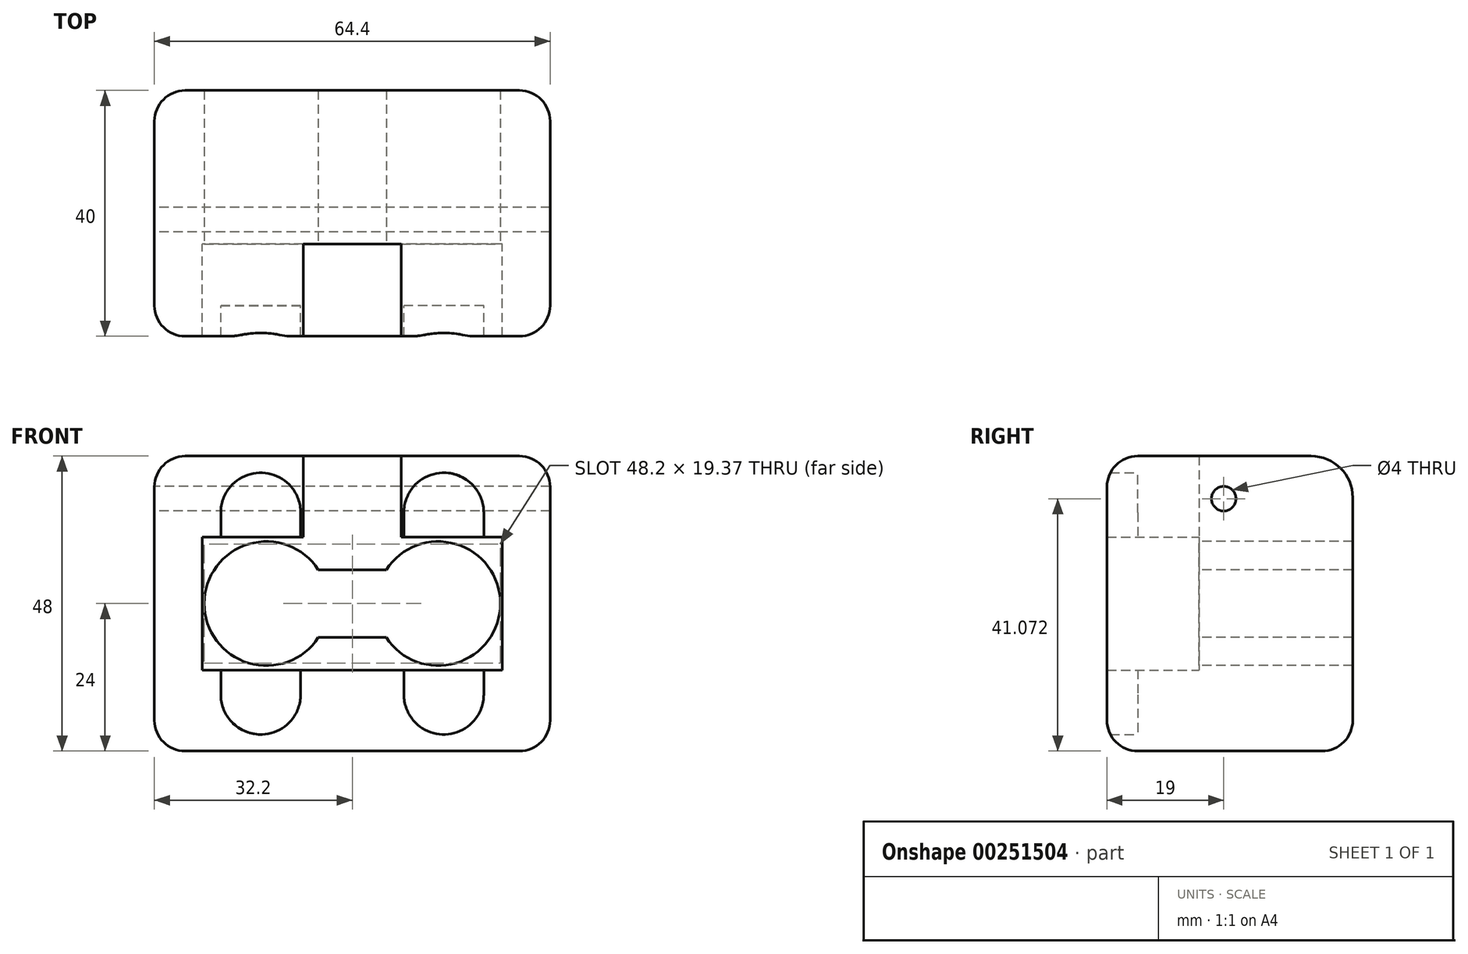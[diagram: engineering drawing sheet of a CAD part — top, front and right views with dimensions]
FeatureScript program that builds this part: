
annotation { "Feature Type Name" : "Feature", "Feature Type Description" : "" }
export const myFeature = defineFeature(function(context is Context, id is Id, definition is map)
    precondition{}
    {
        {
            var Q0;
            Q0=qCreatedBy(makeId("Front.planeOp"),FACE);
            var sketch = newSketch(context, id + "F0", { "sketchPlane" : qUnion([Q0])});
            skLineSegment(sketch, "E0.bottom", {"start": v(32.2, 24) * mm, "end": v(-32.2, 24) * mm});
            skLineSegment(sketch, "E0.top", {"start": v(32.2, -24) * mm, "end": v(-32.2, -24) * mm});
            skLineSegment(sketch, "E0.left", {"start": v(32.2, 24) * mm, "end": v(32.2, -24) * mm});
            skLineSegment(sketch, "E0.right", {"start": v(-32.2, 24) * mm, "end": v(-32.2, -24) * mm});
            skPoint(sketch, "E0.middle", {"position": v(0, 0) * mm});
            skLineSegment(sketch, "E1.bottom", {"start": v(24.4, 10.8) * mm, "end": v(21.4, 10.8) * mm});
            skLineSegment(sketch, "E1.top", {"start": v(24.4, -10.8) * mm, "end": v(21.4, -10.8) * mm});
            skLineSegment(sketch, "E1.left", {"start": v(24.4, 10.8) * mm, "end": v(24.4, -10.8) * mm});
            skLineSegment(sketch, "E1.right", {"start": v(-24.4, 10.8) * mm, "end": v(-24.4, -10.8) * mm});
            skLineSegment(sketch, "E2", {"start": v(-8, 24) * mm, "end": v(-8, 10.8) * mm});
            skPoint(sketch, "E3", {"position": v(0, 24) * mm});
            skLineSegment(sketch, "E4.MirrorCS", {"start": v(8, 24) * mm, "end": v(8, 10.8) * mm});
            skLineSegment(sketch, "E5", {"start": v(-21.4, 10.8) * mm, "end": v(-21.4, 14.8) * mm});
            skLineSegment(sketch, "E6", {"start": v(-8.4, 14.8) * mm, "end": v(-8.4, 10.8) * mm});
            skArc(sketch, "E7", {"start": v(-8.4, 14.8) * mm, "mid": v(-14.9, 21.3) * mm, "end": v(-21.4, 14.8) * mm});
            skLineSegment(sketch, "E8.trimOffspring", {"start": v(-21.4, 10.8) * mm, "end": v(-24.4, 10.8) * mm});
            skLineSegment(sketch, "E9.MirrorCS", {"start": v(21.4, 10.8) * mm, "end": v(21.4, 14.8) * mm});
            skArc(sketch, "E10.MirrorCS", {"start": v(8.4, 14.8) * mm, "mid": v(14.9, 21.3) * mm, "end": v(21.4, 14.8) * mm});
            skLineSegment(sketch, "E11.MirrorCS", {"start": v(8.4, 14.8) * mm, "end": v(8.4, 10.8) * mm});
            skLineSegment(sketch, "E12.MirrorCS", {"start": v(-21.4, -10.8) * mm, "end": v(-21.4, -14.8) * mm});
            skArc(sketch, "E13.MirrorCS", {"start": v(-8.4, -14.8) * mm, "mid": v(-14.9, -21.3) * mm, "end": v(-21.4, -14.8) * mm});
            skLineSegment(sketch, "E14.MirrorCS", {"start": v(-8.4, -14.8) * mm, "end": v(-8.4, -10.8) * mm});
            skLineSegment(sketch, "E15.MirrorCS", {"start": v(8.4, -14.8) * mm, "end": v(8.4, -10.8) * mm});
            skArc(sketch, "E16.MirrorCS", {"start": v(8.4, -14.8) * mm, "mid": v(14.9, -21.3) * mm, "end": v(21.4, -14.8) * mm});
            skLineSegment(sketch, "E17.MirrorCS", {"start": v(21.4, -10.8) * mm, "end": v(21.4, -14.8) * mm});
            skLineSegment(sketch, "E18.trimOffspring", {"start": v(8.4, 10.8) * mm, "end": v(8, 10.8) * mm});
            skLineSegment(sketch, "E19.trimOffspring", {"start": v(8.4, -10.8) * mm, "end": v(-8.4, -10.8) * mm});
            skLineSegment(sketch, "E20.trimOffspring", {"start": v(-21.4, -10.8) * mm, "end": v(-24.4, -10.8) * mm});
            skLineSegment(sketch, "E21.trimOffspring", {"start": v(-8, 10.8) * mm, "end": v(-8.4, 10.8) * mm});
            skSolve(sketch);
        }
        {
            var Q0;
            Q0=makeQuery(id+"F0.imprint","IMPRINT",FACE,{"disambiguationData":[TD([[makeQuery(id+"F0.imprint","IMPRINT",EDGE,{"derivedFrom":sQuery(id+"F0.wireOp",EDGE,"E0.top")}),-1.0]])]});
            extrude(context, id + "F1", {"entities" : qUnion([Q0]), "flatOperationType" : FlatOperationType.REMOVE, "offsetDistance" : 25 * mm, "depth" : 5 * mm, "domain" : OperationDomain.MODEL});
        }
        {
            var Q0;
            Q0=makeQuery(id+"F1.opExtrude","CAP_FACE",FACE,{"disambiguationData":[OSD([sQuery(id+"F0.wireOp",EDGE,"E0.bottom"),sQuery(id+"F0.wireOp",EDGE,"E0.top"),sQuery(id+"F0.wireOp",EDGE,"E0.left"),sQuery(id+"F0.wireOp",EDGE,"E0.right"),sQuery(id+"F0.wireOp",EDGE,"E1.bottom"),sQuery(id+"F0.wireOp",EDGE,"E1.top"),sQuery(id+"F0.wireOp",EDGE,"E1.left"),sQuery(id+"F0.wireOp",EDGE,"E1.right"),sQuery(id+"F0.wireOp",EDGE,"E2"),sQuery(id+"F0.wireOp",EDGE,"E4.MirrorCS"),sQuery(id+"F0.wireOp",EDGE,"E5"),sQuery(id+"F0.wireOp",EDGE,"E6"),sQuery(id+"F0.wireOp",EDGE,"E7"),sQuery(id+"F0.wireOp",EDGE,"E8.trimOffspring"),sQuery(id+"F0.wireOp",EDGE,"E9.MirrorCS"),sQuery(id+"F0.wireOp",EDGE,"E10.MirrorCS"),sQuery(id+"F0.wireOp",EDGE,"E11.MirrorCS"),sQuery(id+"F0.wireOp",EDGE,"E12.MirrorCS"),sQuery(id+"F0.wireOp",EDGE,"E13.MirrorCS"),sQuery(id+"F0.wireOp",EDGE,"E14.MirrorCS"),sQuery(id+"F0.wireOp",EDGE,"E15.MirrorCS"),sQuery(id+"F0.wireOp",EDGE,"E16.MirrorCS"),sQuery(id+"F0.wireOp",EDGE,"E17.MirrorCS"),sQuery(id+"F0.wireOp",EDGE,"E18.trimOffspring"),sQuery(id+"F0.wireOp",EDGE,"E19.trimOffspring"),sQuery(id+"F0.wireOp",EDGE,"E20.trimOffspring"),sQuery(id+"F0.wireOp",EDGE,"E21.trimOffspring")])],"isStart":true});
            var sketch = newSketch(context, id + "F2", { "sketchPlane" : qUnion([Q0])});
            skLineSegment(sketch, "E22.bottom", {"start": v(24.4, -10.8) * mm, "end": v(-24.4, -10.8) * mm});
            skLineSegment(sketch, "E22.top", {"start": v(24.4, 10.8) * mm, "end": v(-24.4, 10.8) * mm});
            skLineSegment(sketch, "E22.left", {"start": v(24.4, -10.8) * mm, "end": v(24.4, 10.8) * mm});
            skLineSegment(sketch, "E22.right", {"start": v(-24.4, -10.8) * mm, "end": v(-24.4, 10.8) * mm});
            skPoint(sketch, "E22.middle", {"position": v(0, 0) * mm});
            skLineSegment(sketch, "E23.bottom", {"start": v(-32.2, 24) * mm, "end": v(32.2, 24) * mm});
            skLineSegment(sketch, "E23.top", {"start": v(-32.2, -24) * mm, "end": v(32.2, -24) * mm});
            skLineSegment(sketch, "E23.left", {"start": v(-32.2, 24) * mm, "end": v(-32.2, -24) * mm});
            skLineSegment(sketch, "E23.right", {"start": v(32.2, 24) * mm, "end": v(32.2, -24) * mm});
            skLineSegment(sketch, "E24", {"start": v(8, 10.8) * mm, "end": v(8, 24) * mm});
            skLineSegment(sketch, "E25", {"start": v(-8, 10.8) * mm, "end": v(-8, 24) * mm});
            skSolve(sketch);
        }
        {
            var Q0;
            {var subQ12=sQuery(id+"F2.wireOp",EDGE,"E22.left");Q0=makeQuery(id+"F2.imprint","IMPRINT",FACE,{"disambiguationData":[TD([[makeQuery(id+"F2.imprint","IMPRINT",EDGE,{"derivedFrom":subQ12}),1.0]])]});}
            var Q1;
            {var subQ1=makeQuery(id+"F1.opExtrude","CAP_EDGE",EDGE,{"disambiguationData":[OSD([sQuery(id+"F0.wireOp",EDGE,"E12.MirrorCS")])],"isStart":true});Q1=makeQuery(id+"F2.imprint","IMPRINT",FACE,{"disambiguationData":[TD([[makeQuery(id+"F2.imprint","IMPRINT",EDGE,{"derivedFrom":subQ1}),-1.0]])]});}
            var Q2;
            {var subQ2=makeQuery(id+"F1.opExtrude","CAP_EDGE",EDGE,{"disambiguationData":[OSD([sQuery(id+"F0.wireOp",EDGE,"E15.MirrorCS")])],"isStart":true});Q2=makeQuery(id+"F2.imprint","IMPRINT",FACE,{"disambiguationData":[TD([[makeQuery(id+"F2.imprint","IMPRINT",EDGE,{"derivedFrom":subQ2}),1.0]])]});}
            var Q3;
            {var subQ1=makeQuery(id+"F1.opExtrude","CAP_EDGE",EDGE,{"disambiguationData":[OSD([sQuery(id+"F0.wireOp",EDGE,"E5")])],"isStart":true});Q3=makeQuery(id+"F2.imprint","IMPRINT",FACE,{"disambiguationData":[TD([[makeQuery(id+"F2.imprint","IMPRINT",EDGE,{"derivedFrom":subQ1}),1.0]])]});}
            var Q4;
            {var subQ1=makeQuery(id+"F1.opExtrude","CAP_EDGE",EDGE,{"disambiguationData":[OSD([sQuery(id+"F0.wireOp",EDGE,"E9.MirrorCS")])],"isStart":true});Q4=makeQuery(id+"F2.imprint","IMPRINT",FACE,{"disambiguationData":[TD([[makeQuery(id+"F2.imprint","IMPRINT",EDGE,{"derivedFrom":subQ1}),-1.0]])]});}
            extrude(context, id + "F3", {"entities" : qUnion([Q0, Q1, Q2, Q3, Q4]), "operationType" : NewBodyOperationType.ADD, "depth" : 10 * mm});
        }
        {
            var Q0;
            Q0=makeQuery(id+"F3.opExtrude","CAP_FACE",FACE,{"disambiguationData":[OSD([sQuery(id+"F2.wireOp",EDGE,"E22.bottom"),sQuery(id+"F2.wireOp",EDGE,"E22.top"),sQuery(id+"F2.wireOp",EDGE,"E22.left"),sQuery(id+"F2.wireOp",EDGE,"E22.right"),sQuery(id+"F2.wireOp",EDGE,"E23.bottom"),sQuery(id+"F2.wireOp",EDGE,"E23.top"),sQuery(id+"F2.wireOp",EDGE,"E23.left"),sQuery(id+"F2.wireOp",EDGE,"E23.right"),sQuery(id+"F2.wireOp",EDGE,"E24"),sQuery(id+"F2.wireOp",EDGE,"E25")])],"isStart":false});
            var sketch = newSketch(context, id + "F4", { "sketchPlane" : qUnion([Q0])});
            skCircle(sketch, "E26", {"center": v(14, 0) * mm, "radius": 10.1 * mm});
            skLineSegment(sketch, "E27", {"start": v(5.53, -5.5) * mm, "end": v(0, -5.5) * mm});
            skLineSegment(sketch, "E28.MirrorCS", {"start": v(5.53, 5.5) * mm, "end": v(0, 5.5) * mm});
            skCircle(sketch, "E29.MirrorC", {"center": v(-14, 0) * mm, "radius": 10.1 * mm});
            skLineSegment(sketch, "E30.MirrorCS", {"start": v(-5.53, -5.5) * mm, "end": v(0, -5.5) * mm});
            skLineSegment(sketch, "E31.MirrorCS", {"start": v(-5.53, 5.5) * mm, "end": v(0, 5.5) * mm});
            skLineSegment(sketch, "E32.bottom", {"start": v(32.2, 24) * mm, "end": v(-32.2, 24) * mm});
            skLineSegment(sketch, "E32.top", {"start": v(32.2, -24) * mm, "end": v(-32.2, -24) * mm});
            skLineSegment(sketch, "E32.left", {"start": v(32.2, 24) * mm, "end": v(32.2, -24) * mm});
            skLineSegment(sketch, "E32.right", {"start": v(-32.2, 24) * mm, "end": v(-32.2, -24) * mm});
            skPoint(sketch, "E32.middle", {"position": v(0, 0) * mm});
            skSolve(sketch);
        }
        {
            var Q0;
            Q0=makeQuery(id+"F4.imprint","IMPRINT",FACE,{"disambiguationData":[TD([[makeQuery(id+"F4.imprint","IMPRINT",EDGE,{"derivedFrom":sQuery(id+"F4.wireOp",EDGE,"E32.top")}),1.0]])]});
            var Q1;
            {var subQ10=sQuery(id+"F4.wireOp",EDGE,"E27");Q1=makeQuery(id+"F4.imprint","IMPRINT",FACE,{"disambiguationData":[TD([[makeQuery(id+"F4.imprint","IMPRINT",EDGE,{"derivedFrom":subQ10}),1.0]])]});}
            extrude(context, id + "F5", {"entities" : qUnion([Q0, Q1]), "operationType" : NewBodyOperationType.ADD, "depth" : 25 * mm});
        }
        {
            var Q0;
            Q0=makeQuery(id+"F5.boolean.opBoolean","MERGE",FACE,{"derivedFrom":[makeQuery(id+"F3.boolean.opBoolean","MERGE",FACE,{"derivedFrom":[makeQuery(id+"F1.opExtrude","SWEPT_FACE",FACE,{"disambiguationData":[OSD([sQuery(id+"F0.wireOp",EDGE,"E0.right")])]}),makeQuery(id+"F3.opExtrude","SWEPT_FACE",FACE,{"disambiguationData":[OSD([sQuery(id+"F2.wireOp",EDGE,"E23.right")])]})]}),makeQuery(id+"F5.opExtrude","SWEPT_FACE",FACE,{"disambiguationData":[OSD([sQuery(id+"F4.wireOp",EDGE,"E32.left")])]})]});
            var sketch = newSketch(context, id + "F6", { "sketchPlane" : qUnion([Q0])});
            skCircle(sketch, "E33", {"center": v(-14, 17.07) * mm, "radius": 2 * mm});
            skCircle(sketch, "E34.MirrorC", {"center": v(-14, 30.93) * mm, "radius": 2 * mm});
            skSolve(sketch);
        }
        {
            var Q0;
            Q0=makeQuery(id+"F5.opExtrude","CAP_EDGE",EDGE,{"disambiguationData":[OSD([sQuery(id+"F4.wireOp",EDGE,"E32.bottom")])],"isStart":false});
            fillet(context, id + "F7", {"entities" : qUnion([Q0]), "radius" : 6.76 * mm, "tangentPropagation" : true, "allowEdgeOverflow" : false});
        }
        {
            var Q0;
            Q0=makeQuery(id+"F6.imprint","IMPRINT",FACE,{"disambiguationData":[TD([[makeQuery(id+"F6.imprint","IMPRINT",EDGE,{"derivedFrom":sQuery(id+"F6.wireOp",EDGE,"E33")}),1.0]])]});
            extrude(context, id + "F8", {"entities" : qUnion([Q0]), "operationType" : NewBodyOperationType.REMOVE, "oppositeDirection" : true, "depth" : 69.4 * mm});
        }
        {
            var Q0;
            Q0=makeQuery(id+"F7.opFillet","BLEND_EDGE",EDGE,{"blendedFrom":[makeQuery(id+"F5.opExtrude","CAP_EDGE",EDGE,{"disambiguationData":[OSD([sQuery(id+"F4.wireOp",EDGE,"E32.bottom")])],"isStart":false}),makeQuery(id+"F5.boolean.opBoolean","MERGE",FACE,{"derivedFrom":[makeQuery(id+"F3.boolean.opBoolean","MERGE",FACE,{"derivedFrom":[makeQuery(id+"F1.opExtrude","SWEPT_FACE",FACE,{"disambiguationData":[OSD([sQuery(id+"F0.wireOp",EDGE,"E0.left")])]}),makeQuery(id+"F3.opExtrude","SWEPT_FACE",FACE,{"disambiguationData":[OSD([sQuery(id+"F2.wireOp",EDGE,"E23.left")])]})]}),makeQuery(id+"F5.opExtrude","SWEPT_FACE",FACE,{"disambiguationData":[OSD([sQuery(id+"F4.wireOp",EDGE,"E32.right")])]})]})],"blendedInto":[makeQuery(id+"F5.boolean.opBoolean","MERGE",FACE,{"derivedFrom":[makeQuery(id+"F3.boolean.opBoolean","MERGE",FACE,{"derivedFrom":[makeQuery(id+"F1.opExtrude","SWEPT_FACE",FACE,{"disambiguationData":[OSD([sQuery(id+"F0.wireOp",EDGE,"E0.left")])]}),makeQuery(id+"F3.opExtrude","SWEPT_FACE",FACE,{"disambiguationData":[OSD([sQuery(id+"F2.wireOp",EDGE,"E23.left")])]})]}),makeQuery(id+"F5.opExtrude","SWEPT_FACE",FACE,{"disambiguationData":[OSD([sQuery(id+"F4.wireOp",EDGE,"E32.right")])]})]})]});
            var Q1;
            Q1=makeQuery(id+"F5.opExtrude","CAP_EDGE",EDGE,{"disambiguationData":[OSD([sQuery(id+"F4.wireOp",EDGE,"E32.right")])],"isStart":false});
            fillet(context, id + "F9", {"entities" : qUnion([Q0, Q1]), "radius" : 5 * mm, "tangentPropagation" : true, "allowEdgeOverflow" : false});
        }
        {
            var Q0;
            Q0=makeQuery(id+"F5.opExtrude","CAP_EDGE",EDGE,{"disambiguationData":[OSD([sQuery(id+"F4.wireOp",EDGE,"E32.left")])],"isStart":false});
            fillet(context, id + "F10", {"entities" : qUnion([Q0]), "radius" : 5 * mm, "tangentPropagation" : true, "allowEdgeOverflow" : false});
        }
        {
            var Q0;
            {var subQ0=sQuery(id+"F0.wireOp",EDGE,"E0.bottom");Q0=makeQuery(id+"F1.opExtrude","CAP_EDGE",EDGE,{"disambiguationData":[OSD([subQ0]),TDD([makeQuery(id+"F0.imprint","IMPRINT",EDGE,{"disambiguationData":[TD([[makeQuery(id+"F0.imprint","INTERSECT",VERTEX,{"derivedFrom":[subQ0,sQuery(id+"F0.wireOp",EDGE,"E0.right")]}),1.0]])],"derivedFrom":subQ0})])],"isStart":false});}
            var Q1;
            {var subQ0=sQuery(id+"F0.wireOp",EDGE,"E0.bottom");Q1=makeQuery(id+"F1.opExtrude","CAP_EDGE",EDGE,{"disambiguationData":[OSD([subQ0]),TDD([makeQuery(id+"F0.imprint","IMPRINT",EDGE,{"disambiguationData":[TD([[makeQuery(id+"F0.imprint","INTERSECT",VERTEX,{"derivedFrom":[subQ0,sQuery(id+"F0.wireOp",EDGE,"E0.left")]}),-1.0]])],"derivedFrom":subQ0})])],"isStart":false});}
            fillet(context, id + "F11", {"entities" : qUnion([Q0, Q1]), "radius" : 5 * mm, "tangentPropagation" : true, "allowEdgeOverflow" : false});
        }
        {
            var Q0;
            Q0=makeQuery(id+"F5.boolean.opBoolean","MERGE",FACE,{"derivedFrom":[makeQuery(id+"F3.boolean.opBoolean","MERGE",FACE,{"derivedFrom":[makeQuery(id+"F1.opExtrude","SWEPT_FACE",FACE,{"disambiguationData":[OSD([sQuery(id+"F0.wireOp",EDGE,"E0.top")])]}),makeQuery(id+"F3.opExtrude","SWEPT_FACE",FACE,{"disambiguationData":[OSD([sQuery(id+"F2.wireOp",EDGE,"E23.top")])]})]}),makeQuery(id+"F5.opExtrude","SWEPT_FACE",FACE,{"disambiguationData":[OSD([sQuery(id+"F4.wireOp",EDGE,"E32.top")])]})]});
            fillet(context, id + "F12", {"entities" : qUnion([Q0]), "radius" : 5 * mm, "tangentPropagation" : true, "allowEdgeOverflow" : false});
        }
    });
